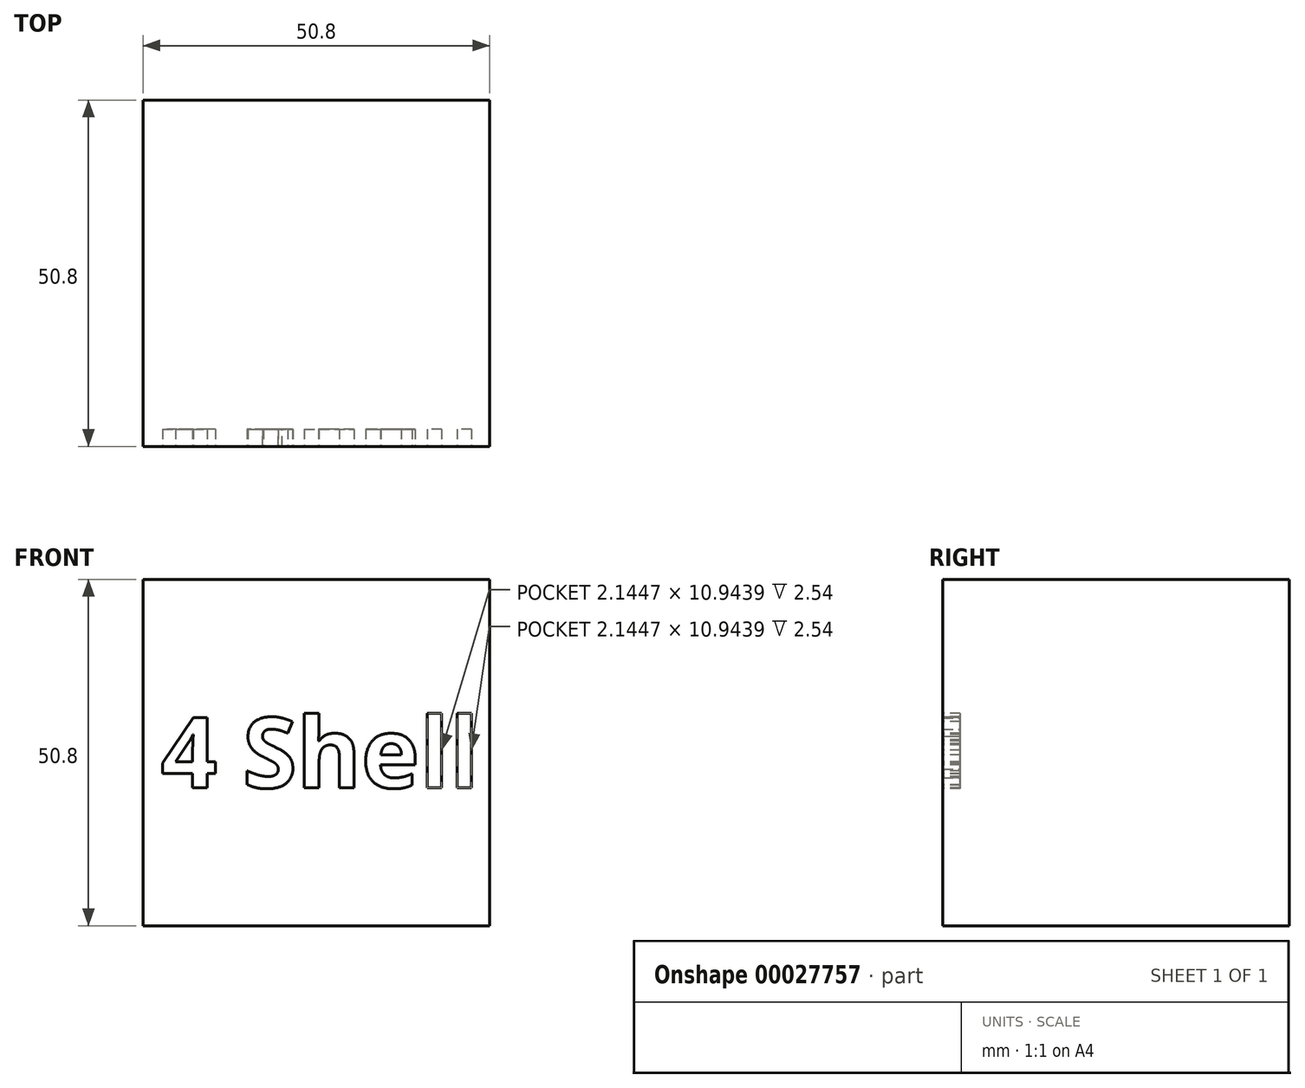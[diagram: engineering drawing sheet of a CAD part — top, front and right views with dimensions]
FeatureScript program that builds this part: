
annotation { "Feature Type Name" : "Feature", "Feature Type Description" : "" }
export const myFeature = defineFeature(function(context is Context, id is Id, definition is map)
    precondition{}
    {
        {
            var Q0;
            Q0=qCreatedBy(makeId("Top.planeOp"),FACE);
            var sketch = newSketch(context, id + "F0", { "sketchPlane" : qUnion([Q0])});
            skLineSegment(sketch, "E0.bottom", {"start": v(0, 0) * mm, "end": v(50.8, 0) * mm});
            skLineSegment(sketch, "E0.top", {"start": v(0, 50.8) * mm, "end": v(50.8, 50.8) * mm});
            skLineSegment(sketch, "E0.left", {"start": v(0, 0) * mm, "end": v(0, 50.8) * mm});
            skLineSegment(sketch, "E0.right", {"start": v(50.8, 0) * mm, "end": v(50.8, 50.8) * mm});
            skSolve(sketch);
        }
        {
            var Q0;
            Q0=makeQuery(id+"F0.imprint","IMPRINT",FACE,{"disambiguationData":[TD([[makeQuery(id+"F0.imprint","IMPRINT",EDGE,{"derivedFrom":sQuery(id+"F0.wireOp",EDGE,"E0.bottom")}),1.0]])]});
            extrude(context, id + "F1", {"entities" : qUnion([Q0]), "depth" : 50.8 * mm});
        }
        {
            var Q0;
            Q0=makeQuery(id+"F1.opExtrude","SWEPT_FACE",FACE,{"disambiguationData":[OSD([sQuery(id+"F0.wireOp",EDGE,"E0.bottom")])]});
            var sketch = newSketch(context, id + "F2", { "sketchPlane" : qUnion([Q0])});
            skText(sketch, "E1", { "text": "4 Shell", "fontName": "OpenSans-Bold.ttf"});
            skLineSegment(sketch, "E2", {"start": v(2.64, 25.4) * mm, "end": v(48.16, 25.4) * mm, "construction": true});
            const initialGuessF2  = {"E1": [0.00264, 0.02022, 1, 0, 0.01037]};
            skSetInitialGuess(sketch, initialGuessF2);
            skSolve(sketch);
        }
        {
            var Q0;
            Q0 = qSketchRegion(id + "F2", true);
            extrude(context, id + "F3", {"entities" : qUnion([Q0]), "operationType" : NewBodyOperationType.REMOVE, "oppositeDirection" : true, "depth" : 2.54 * mm});
        }
    });
